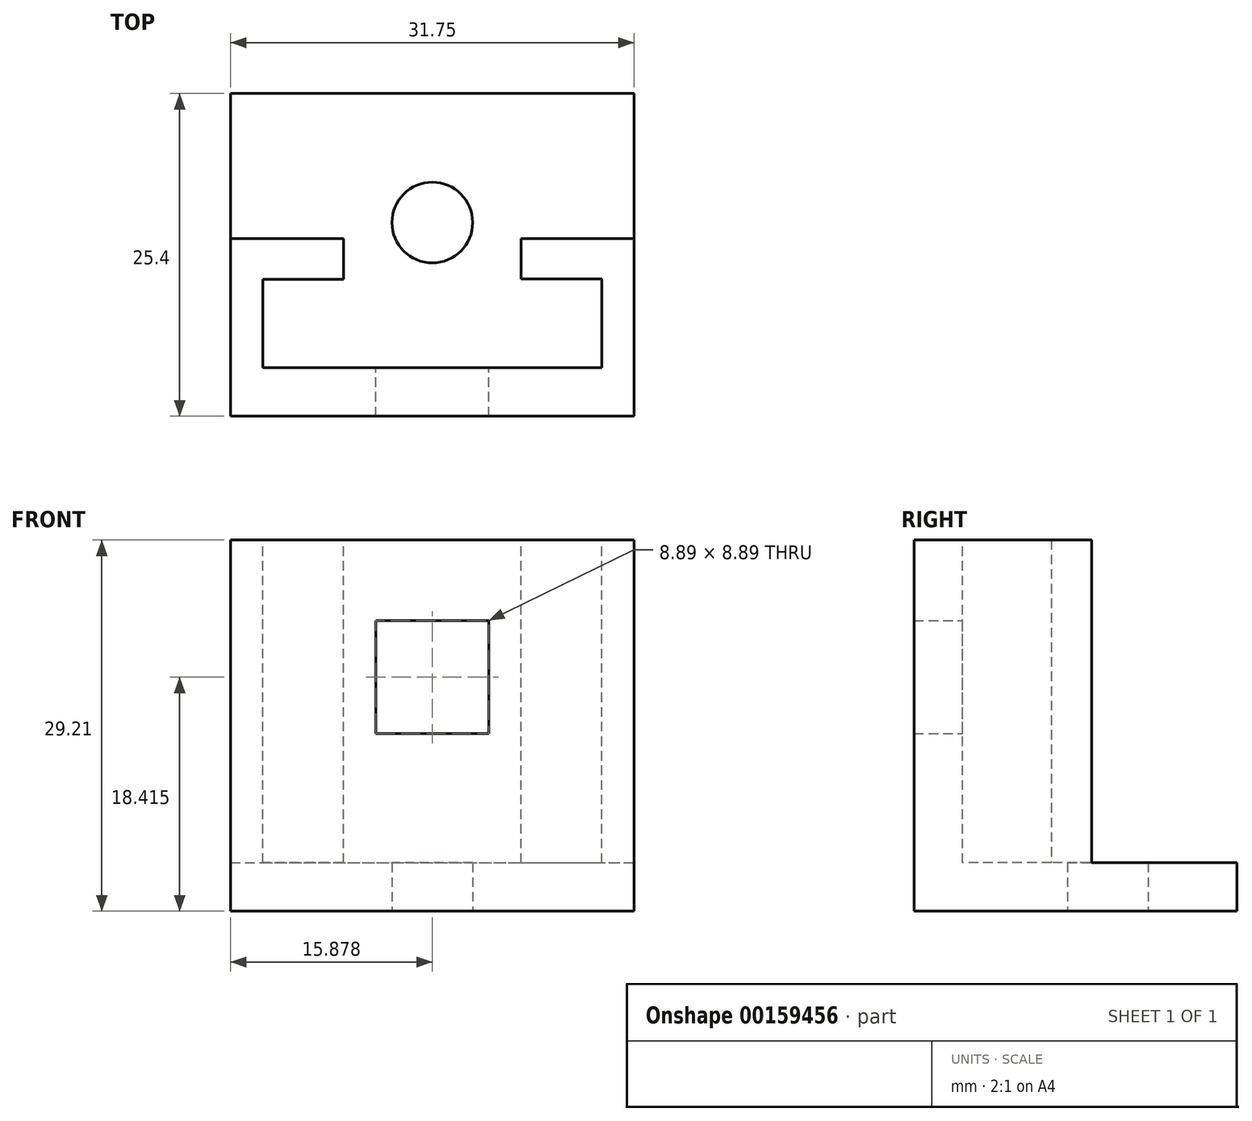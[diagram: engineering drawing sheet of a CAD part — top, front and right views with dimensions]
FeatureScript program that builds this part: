
annotation { "Feature Type Name" : "Feature", "Feature Type Description" : "" }
export const myFeature = defineFeature(function(context is Context, id is Id, definition is map)
    precondition{}
    {
        {
            var Q0;
            Q0=qCreatedBy(makeId("Top.planeOp"),FACE);
            var sketch = newSketch(context, id + "F0", { "sketchPlane" : qUnion([Q0])});
            skLineSegment(sketch, "E0.bottom", {"start": v(-27.54, 42.04) * mm, "end": v(4.21, 42.04) * mm});
            skLineSegment(sketch, "E0.top", {"start": v(-27.54, 16.64) * mm, "end": v(4.21, 16.64) * mm});
            skLineSegment(sketch, "E0.left", {"start": v(-27.54, 42.04) * mm, "end": v(-27.54, 16.64) * mm});
            skLineSegment(sketch, "E0.right", {"start": v(4.21, 42.04) * mm, "end": v(4.21, 16.64) * mm});
            skLineSegment(sketch, "E1", {"start": v(4.21, 31.88) * mm, "end": v(-27.54, 31.88) * mm, "construction": true});
            skPoint(sketch, "E1.endSnap0", {"position": v(-27.54, 29.34) * mm});
            skCircle(sketch, "E2", {"center": v(-11.66, 31.88) * mm, "radius": 3.18 * mm});
            skSolve(sketch);
        }
        {
            var Q0;
            Q0=makeQuery(id+"F0.imprint","IMPRINT",FACE,{"disambiguationData":[TD([[makeQuery(id+"F0.imprint","IMPRINT",EDGE,{"derivedFrom":sQuery(id+"F0.wireOp",EDGE,"E0.bottom")}),-1.0]])]});
            extrude(context, id + "F1", {"entities" : qUnion([Q0]), "depth" : 3.8 * mm});
        }
        {
            var Q0;
            Q0=makeQuery(id+"F1.opExtrude","CAP_FACE",FACE,{"disambiguationData":[OSD([sQuery(id+"F0.wireOp",EDGE,"E0.bottom"),sQuery(id+"F0.wireOp",EDGE,"E0.top"),sQuery(id+"F0.wireOp",EDGE,"E0.left"),sQuery(id+"F0.wireOp",EDGE,"E0.right"),sQuery(id+"F0.wireOp",EDGE,"l3L2diFd-Amgv-pFva-WlLd-QlazSRAwc6tV")])],"isStart":false});
            var sketch = newSketch(context, id + "F2", { "sketchPlane" : qUnion([Q0])});
            skLineSegment(sketch, "E3.bottom", {"start": v(-27.54, 16.64) * mm, "end": v(4.21, 16.64) * mm});
            skLineSegment(sketch, "E3.top", {"start": v(-27.54, 20.45) * mm, "end": v(4.21, 20.45) * mm});
            skLineSegment(sketch, "E3.left", {"start": v(-27.54, 16.64) * mm, "end": v(-27.54, 20.45) * mm});
            skLineSegment(sketch, "E3.right", {"start": v(4.21, 16.64) * mm, "end": v(4.21, 20.45) * mm});
            skSolve(sketch);
        }
        {
            var Q0;
            Q0=makeQuery(id+"F2.imprint","IMPRINT",FACE,{"disambiguationData":[TD([[makeQuery(id+"F2.imprint","IMPRINT",EDGE,{"derivedFrom":sQuery(id+"F2.wireOp",EDGE,"E3.bottom")}),1.0]])]});
            extrude(context, id + "F3", {"entities" : qUnion([Q0]), "operationType" : NewBodyOperationType.ADD, "depth" : 25.4 * mm});
        }
        {
            var Q0;
            Q0=makeQuery(id+"F3.opExtrude","SWEPT_FACE",FACE,{"disambiguationData":[OSD([sQuery(id+"F2.wireOp",EDGE,"E3.top")])]});
            var sketch = newSketch(context, id + "F4", { "sketchPlane" : qUnion([Q0])});
            skLineSegment(sketch, "E4.bottom", {"start": v(-4.21, 3.81) * mm, "end": v(-1.67, 3.81) * mm});
            skLineSegment(sketch, "E4.top", {"start": v(-4.21, 29.21) * mm, "end": v(-1.67, 29.21) * mm});
            skLineSegment(sketch, "E4.left", {"start": v(-4.21, 3.81) * mm, "end": v(-4.21, 29.21) * mm});
            skLineSegment(sketch, "E4.right", {"start": v(-1.67, 3.81) * mm, "end": v(-1.67, 29.21) * mm});
            skLineSegment(sketch, "E5.bottom", {"start": v(27.54, 3.81) * mm, "end": v(25, 3.81) * mm});
            skLineSegment(sketch, "E5.top", {"start": v(27.54, 29.21) * mm, "end": v(25, 29.21) * mm});
            skLineSegment(sketch, "E5.left", {"start": v(27.54, 3.81) * mm, "end": v(27.54, 29.21) * mm});
            skLineSegment(sketch, "E5.right", {"start": v(25, 3.81) * mm, "end": v(25, 29.21) * mm});
            skLineSegment(sketch, "E6", {"start": v(11.66, 3.81) * mm, "end": v(11.66, 29.21) * mm, "construction": true});
            skLineSegment(sketch, "E7.bottom", {"start": v(16.1, 13.97) * mm, "end": v(7.22, 13.97) * mm});
            skLineSegment(sketch, "E7.top", {"start": v(16.1, 22.86) * mm, "end": v(7.22, 22.86) * mm});
            skLineSegment(sketch, "E7.left", {"start": v(16.1, 13.97) * mm, "end": v(16.1, 22.86) * mm});
            skLineSegment(sketch, "E7.right", {"start": v(7.22, 13.97) * mm, "end": v(7.22, 22.86) * mm});
            skPoint(sketch, "E7.middle", {"position": v(11.66, 18.42) * mm});
            skSolve(sketch);
        }
        {
            var Q0;
            Q0=makeQuery(id+"F4.imprint","IMPRINT",FACE,{"disambiguationData":[TD([[makeQuery(id+"F4.imprint","IMPRINT",EDGE,{"derivedFrom":sQuery(id+"F4.wireOp",EDGE,"E4.bottom")}),-1.0]])]});
            var Q1;
            Q1=makeQuery(id+"F4.imprint","IMPRINT",FACE,{"disambiguationData":[TD([[makeQuery(id+"F4.imprint","IMPRINT",EDGE,{"derivedFrom":sQuery(id+"F4.wireOp",EDGE,"E5.bottom")}),-1.0]])]});
            extrude(context, id + "F5", {"entities" : qUnion([Q0, Q1]), "operationType" : NewBodyOperationType.ADD, "depth" : 10.16 * mm});
        }
        {
            var Q0;
            Q0=makeQuery(id+"F4.imprint","IMPRINT",FACE,{"disambiguationData":[TD([[makeQuery(id+"F4.imprint","IMPRINT",EDGE,{"derivedFrom":sQuery(id+"F4.wireOp",EDGE,"E7.bottom")}),-1.0]])]});
            extrude(context, id + "F6", {"entities" : qUnion([Q0]), "operationType" : NewBodyOperationType.REMOVE, "oppositeDirection" : true, "depth" : 25.4 * mm});
        }
        {
            var Q0;
            Q0=makeQuery(id+"F5.opExtrude","SWEPT_FACE",FACE,{"disambiguationData":[OSD([sQuery(id+"F4.wireOp",EDGE,"E5.right")])]});
            var sketch = newSketch(context, id + "F7", { "sketchPlane" : qUnion([Q0])});
            skLineSegment(sketch, "E8.bottom", {"start": v(30.61, 29.21) * mm, "end": v(27.43, 29.21) * mm});
            skLineSegment(sketch, "E8.top", {"start": v(30.61, 3.8) * mm, "end": v(27.43, 3.8) * mm});
            skLineSegment(sketch, "E8.left", {"start": v(30.61, 29.21) * mm, "end": v(30.61, 3.8) * mm});
            skLineSegment(sketch, "E8.right", {"start": v(27.43, 29.21) * mm, "end": v(27.43, 3.8) * mm});
            skSolve(sketch);
        }
        {
            var Q0;
            Q0=makeQuery(id+"F5.opExtrude","SWEPT_FACE",FACE,{"disambiguationData":[OSD([sQuery(id+"F4.wireOp",EDGE,"E4.right")])]});
            var sketch = newSketch(context, id + "F8", { "sketchPlane" : qUnion([Q0])});
            skLineSegment(sketch, "E9.bottom", {"start": v(-30.61, 29.21) * mm, "end": v(-27.44, 29.21) * mm});
            skLineSegment(sketch, "E9.top", {"start": v(-30.61, 3.81) * mm, "end": v(-27.44, 3.81) * mm});
            skLineSegment(sketch, "E9.left", {"start": v(-30.61, 29.21) * mm, "end": v(-30.61, 3.81) * mm});
            skLineSegment(sketch, "E9.right", {"start": v(-27.44, 29.21) * mm, "end": v(-27.44, 3.81) * mm});
            skSolve(sketch);
        }
        {
            var Q0;
            Q0=makeQuery(id+"F8.imprint","IMPRINT",FACE,{"disambiguationData":[TD([[makeQuery(id+"F8.imprint","IMPRINT",EDGE,{"derivedFrom":sQuery(id+"F8.wireOp",EDGE,"E9.bottom")}),-1.0]])]});
            extrude(context, id + "F9", {"entities" : qUnion([Q0]), "operationType" : NewBodyOperationType.ADD, "depth" : 6.35 * mm});
        }
        {
            var Q0;
            Q0=makeQuery(id+"F7.imprint","IMPRINT",FACE,{"disambiguationData":[TD([[makeQuery(id+"F7.imprint","IMPRINT",EDGE,{"derivedFrom":sQuery(id+"F7.wireOp",EDGE,"E8.bottom")}),1.0]])]});
            extrude(context, id + "F10", {"entities" : qUnion([Q0]), "operationType" : NewBodyOperationType.ADD, "depth" : 6.35 * mm});
        }
    });
